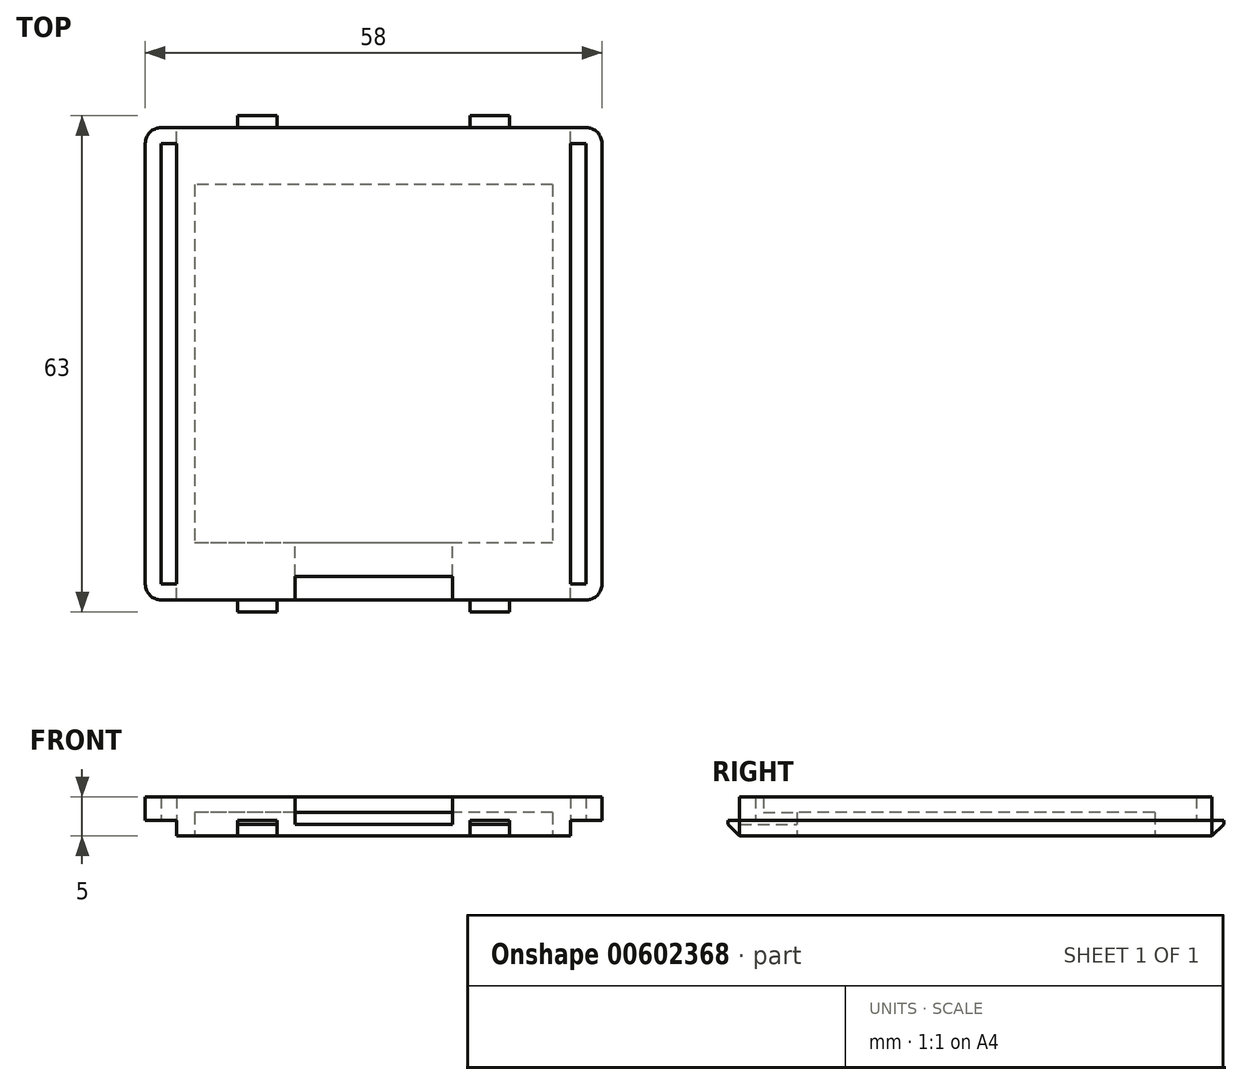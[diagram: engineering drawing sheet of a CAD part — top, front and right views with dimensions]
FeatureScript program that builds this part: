
annotation { "Feature Type Name" : "Feature", "Feature Type Description" : "" }
export const myFeature = defineFeature(function(context is Context, id is Id, definition is map)
    precondition{}
    {
        {
            var Q0;
            Q0=qCreatedBy(makeId("Top.planeOp"),FACE);
            var sketch = newSketch(context, id + "F0", { "sketchPlane" : qUnion([Q0])});
            skLineSegment(sketch, "E0.bottom", {"start": v(25, -30) * mm, "end": v(-25, -30) * mm});
            skLineSegment(sketch, "E0.top", {"start": v(25, 30) * mm, "end": v(-25, 30) * mm});
            skLineSegment(sketch, "E0.left", {"start": v(25, -30) * mm, "end": v(25, 30) * mm});
            skLineSegment(sketch, "E0.right", {"start": v(-25, -30) * mm, "end": v(-25, 30) * mm});
            skPoint(sketch, "E0.middle", {"position": v(0, 0) * mm});
            skSolve(sketch);
        }
        {
            var Q0;
            Q0=qSketchRegion(id+"F0",true);
            extrude(context, id + "F1", {"entities" : qUnion([Q0]), "depth" : 5 * mm, "offsetDistance" : 25 * mm});
        }
        {
            var Q0;
            Q0=qCreatedBy(makeId("Top.planeOp"),FACE);
            var sketch = newSketch(context, id + "F2", { "sketchPlane" : qUnion([Q0])});
            skLineSegment(sketch, "E1.bottom", {"start": v(22.75, 22.75) * mm, "end": v(-22.75, 22.75) * mm});
            skLineSegment(sketch, "E1.top", {"start": v(22.75, -22.75) * mm, "end": v(-22.75, -22.75) * mm});
            skLineSegment(sketch, "E1.left", {"start": v(22.75, 22.75) * mm, "end": v(22.75, -22.75) * mm});
            skLineSegment(sketch, "E1.right", {"start": v(-22.75, 22.75) * mm, "end": v(-22.75, -22.75) * mm});
            skPoint(sketch, "E1.middle", {"position": v(0, 0) * mm});
            skSolve(sketch);
        }
        {
            var Q0;
            Q0=qCreatedBy(makeId("Top.planeOp"),FACE);
            var sketch = newSketch(context, id + "F3", { "sketchPlane" : qUnion([Q0])});
            skLineSegment(sketch, "E2.bottom", {"start": v(29, 30) * mm, "end": v(-29, 30) * mm});
            skLineSegment(sketch, "E2.top", {"start": v(29, -30) * mm, "end": v(-29, -30) * mm});
            skLineSegment(sketch, "E2.left", {"start": v(29, 30) * mm, "end": v(29, -30) * mm});
            skLineSegment(sketch, "E2.right", {"start": v(-29, 30) * mm, "end": v(-29, -30) * mm});
            skPoint(sketch, "E2.middle", {"position": v(0, 0) * mm});
            skSolve(sketch);
        }
        {
            var Q0;
            Q0=makeQuery(id+"F3.imprint","IMPRINT",FACE,{"disambiguationData":[TD([[makeQuery(id+"F3.imprint","IMPRINT",EDGE,{"derivedFrom":sQuery(id+"F3.wireOp",EDGE,"E2.bottom")}),1.0]])]});
            extrude(context, id + "F4", {"entities" : qUnion([Q0]), "operationType" : NewBodyOperationType.ADD, "depth" : 5 * mm, "offsetDistance" : 25 * mm, "hasSecondDirection" : true, "secondDirectionOppositeDirection" : false, "secondDirectionDepth" : 2 * mm});
        }
        {
            var Q0;
            Q0=qSketchRegion(id+"F2",true);
            extrude(context, id + "F5", {"entities" : qUnion([Q0]), "operationType" : NewBodyOperationType.REMOVE, "depth" : 3 * mm, "offsetDistance" : 25 * mm});
        }
        {
            var Q0;
            Q0=qCreatedBy(makeId("Top.planeOp"),FACE);
            var sketch = newSketch(context, id + "F6", { "sketchPlane" : qUnion([Q0])});
            skLineSegment(sketch, "E3.bottom", {"start": v(10, -30) * mm, "end": v(-10, -30) * mm});
            skLineSegment(sketch, "E3.top", {"start": v(10, 0) * mm, "end": v(-10, 0) * mm});
            skLineSegment(sketch, "E3.left", {"start": v(10, -30) * mm, "end": v(10, 0) * mm});
            skLineSegment(sketch, "E3.right", {"start": v(-10, -30) * mm, "end": v(-10, 0) * mm});
            skPoint(sketch, "E3.middle", {"position": v(0, -15) * mm});
            skSolve(sketch);
        }
        {
            var Q0;
            Q0=qSketchRegion(id+"F6",true);
            extrude(context, id + "F7", {"entities" : qUnion([Q0]), "operationType" : NewBodyOperationType.REMOVE, "depth" : 3 * mm, "offsetDistance" : 25 * mm, "hasSecondDirection" : true, "secondDirectionOppositeDirection" : false, "secondDirectionDepth" : 1.5 * mm});
        }
        {
            var Q0;
            Q0=qCreatedBy(makeId("Top.planeOp"),FACE);
            var sketch = newSketch(context, id + "F8", { "sketchPlane" : qUnion([Q0])});
            skLineSegment(sketch, "E4.bottom", {"start": v(-25, 28) * mm, "end": v(-27, 28) * mm});
            skLineSegment(sketch, "E4.top", {"start": v(-25, -28) * mm, "end": v(-27, -28) * mm});
            skLineSegment(sketch, "E4.left", {"start": v(-25, 28) * mm, "end": v(-25, -28) * mm});
            skLineSegment(sketch, "E4.right", {"start": v(-27, 28) * mm, "end": v(-27, -28) * mm});
            skLineSegment(sketch, "E5.bottom", {"start": v(25, 28) * mm, "end": v(27, 28) * mm});
            skLineSegment(sketch, "E5.top", {"start": v(25, -28) * mm, "end": v(27, -28) * mm});
            skLineSegment(sketch, "E5.left", {"start": v(25, 28) * mm, "end": v(25, -28) * mm});
            skLineSegment(sketch, "E5.right", {"start": v(27, 28) * mm, "end": v(27, -28) * mm});
            skSolve(sketch);
        }
        {
            var Q0;
            Q0=qSketchRegion(id+"F8",true);
            extrude(context, id + "F9", {"entities" : qUnion([Q0]), "operationType" : NewBodyOperationType.REMOVE, "depth" : 25 * mm, "offsetDistance" : 25 * mm});
        }
        {
            var Q0;
            Q0=makeQuery(id+"F4.opExtrude","SWEPT_EDGE",EDGE,{"disambiguationData":[OSD([sQuery(id+"F3.wireOp",EDGE,"E2.top"),sQuery(id+"F3.wireOp",EDGE,"E2.left")])]});
            var Q1;
            Q1=makeQuery(id+"F4.opExtrude","SWEPT_EDGE",EDGE,{"disambiguationData":[OSD([sQuery(id+"F3.wireOp",EDGE,"E2.top"),sQuery(id+"F3.wireOp",EDGE,"E2.right")])]});
            var Q2;
            Q2=makeQuery(id+"F4.opExtrude","SWEPT_EDGE",EDGE,{"disambiguationData":[OSD([sQuery(id+"F3.wireOp",EDGE,"E2.bottom"),sQuery(id+"F3.wireOp",EDGE,"E2.right")])]});
            var Q3;
            Q3=makeQuery(id+"F4.opExtrude","SWEPT_EDGE",EDGE,{"disambiguationData":[OSD([sQuery(id+"F3.wireOp",EDGE,"E2.bottom"),sQuery(id+"F3.wireOp",EDGE,"E2.left")])]});
            fillet(context, id + "F10", {"entities" : qUnion([Q0, Q1, Q2, Q3]), "radius" : 2 * mm, "tangentPropagation" : true, "allowEdgeOverflow" : false});
        }
        {
            var Q0;
            Q0=qCreatedBy(makeId("Top.planeOp"),FACE);
            var sketch = newSketch(context, id + "F11", { "sketchPlane" : qUnion([Q0])});
            skLineSegment(sketch, "E6.bottom", {"start": v(-17.25, -30) * mm, "end": v(-12.25, -30) * mm});
            skLineSegment(sketch, "E6.top", {"start": v(-17.25, -31.5) * mm, "end": v(-12.25, -31.5) * mm});
            skLineSegment(sketch, "E6.left", {"start": v(-17.25, -30) * mm, "end": v(-17.25, -31.5) * mm});
            skLineSegment(sketch, "E6.right", {"start": v(-12.25, -30) * mm, "end": v(-12.25, -31.5) * mm});
            skLineSegment(sketch, "E7.MirrorCS", {"start": v(17.25, -30) * mm, "end": v(12.25, -30) * mm});
            skLineSegment(sketch, "E8.MirrorCS", {"start": v(17.25, -31.5) * mm, "end": v(12.25, -31.5) * mm});
            skLineSegment(sketch, "E9.MirrorCS", {"start": v(17.25, -30) * mm, "end": v(17.25, -31.5) * mm});
            skLineSegment(sketch, "E10.MirrorCS", {"start": v(12.25, -30) * mm, "end": v(12.25, -31.5) * mm});
            skLineSegment(sketch, "E11.MirrorCS", {"start": v(12.25, 30) * mm, "end": v(12.25, 31.5) * mm});
            skLineSegment(sketch, "E12.MirrorCS", {"start": v(17.25, 30) * mm, "end": v(17.25, 31.5) * mm});
            skLineSegment(sketch, "E13.MirrorCS", {"start": v(-12.25, 30) * mm, "end": v(-12.25, 31.5) * mm});
            skLineSegment(sketch, "E14.MirrorCS", {"start": v(-17.25, 30) * mm, "end": v(-17.25, 31.5) * mm});
            skLineSegment(sketch, "E15.MirrorCS", {"start": v(17.25, 31.5) * mm, "end": v(12.25, 31.5) * mm});
            skLineSegment(sketch, "E16.MirrorCS", {"start": v(-17.25, 31.5) * mm, "end": v(-12.25, 31.5) * mm});
            skLineSegment(sketch, "E17.MirrorCS", {"start": v(-17.25, 30) * mm, "end": v(-12.25, 30) * mm});
            skLineSegment(sketch, "E18.MirrorCS", {"start": v(17.25, 30) * mm, "end": v(12.25, 30) * mm});
            skSolve(sketch);
        }
        {
            var Q0;
            Q0=qSketchRegion(id+"F11",true);
            extrude(context, id + "F12", {"entities" : qUnion([Q0]), "operationType" : NewBodyOperationType.ADD, "depth" : 2 * mm, "offsetDistance" : 25 * mm});
        }
        {
            var Q0;
            Q0=makeQuery(id+"F12.opExtrude","CAP_EDGE",EDGE,{"disambiguationData":[OSD([sQuery(id+"F11.wireOp",EDGE,"E6.top")])],"isStart":true});
            var Q1;
            Q1=makeQuery(id+"F12.opExtrude","CAP_EDGE",EDGE,{"disambiguationData":[OSD([sQuery(id+"F11.wireOp",EDGE,"E8.MirrorCS")])],"isStart":true});
            var Q2;
            Q2=makeQuery(id+"F12.opExtrude","CAP_EDGE",EDGE,{"disambiguationData":[OSD([sQuery(id+"F11.wireOp",EDGE,"E15.MirrorCS")])],"isStart":true});
            var Q3;
            Q3=makeQuery(id+"F12.opExtrude","CAP_EDGE",EDGE,{"disambiguationData":[OSD([sQuery(id+"F11.wireOp",EDGE,"E16.MirrorCS")])],"isStart":true});
            chamfer(context, id + "F13", {"entities" : qUnion([Q0, Q1, Q2, Q3]), "width" : 1.5 * mm, "tangentPropagation" : true});
        }
        {
            var Q0;
            Q0=qCreatedBy(makeId("Top.planeOp"),FACE);
            var sketch = newSketch(context, id + "F14", { "sketchPlane" : qUnion([Q0])});
            skLineSegment(sketch, "E19.bottom", {"start": v(10, -30) * mm, "end": v(-10, -30) * mm});
            skLineSegment(sketch, "E19.top", {"start": v(10, -27) * mm, "end": v(-10, -27) * mm});
            skLineSegment(sketch, "E19.left", {"start": v(10, -30) * mm, "end": v(10, -27) * mm});
            skLineSegment(sketch, "E19.right", {"start": v(-10, -30) * mm, "end": v(-10, -27) * mm});
            skPoint(sketch, "E19.middle", {"position": v(0, -28.5) * mm});
            skSolve(sketch);
        }
        {
            var Q0;
            Q0 = qSketchRegion(id + "F14", true);
            extrude(context, id + "F15", {"entities" : qUnion([Q0]), "operationType" : NewBodyOperationType.REMOVE, "depth" : 5 * mm, "offsetDistance" : 25 * mm, "hasSecondDirection" : true, "secondDirectionOppositeDirection" : false, "secondDirectionDepth" : 3 * mm});
        }
    });
